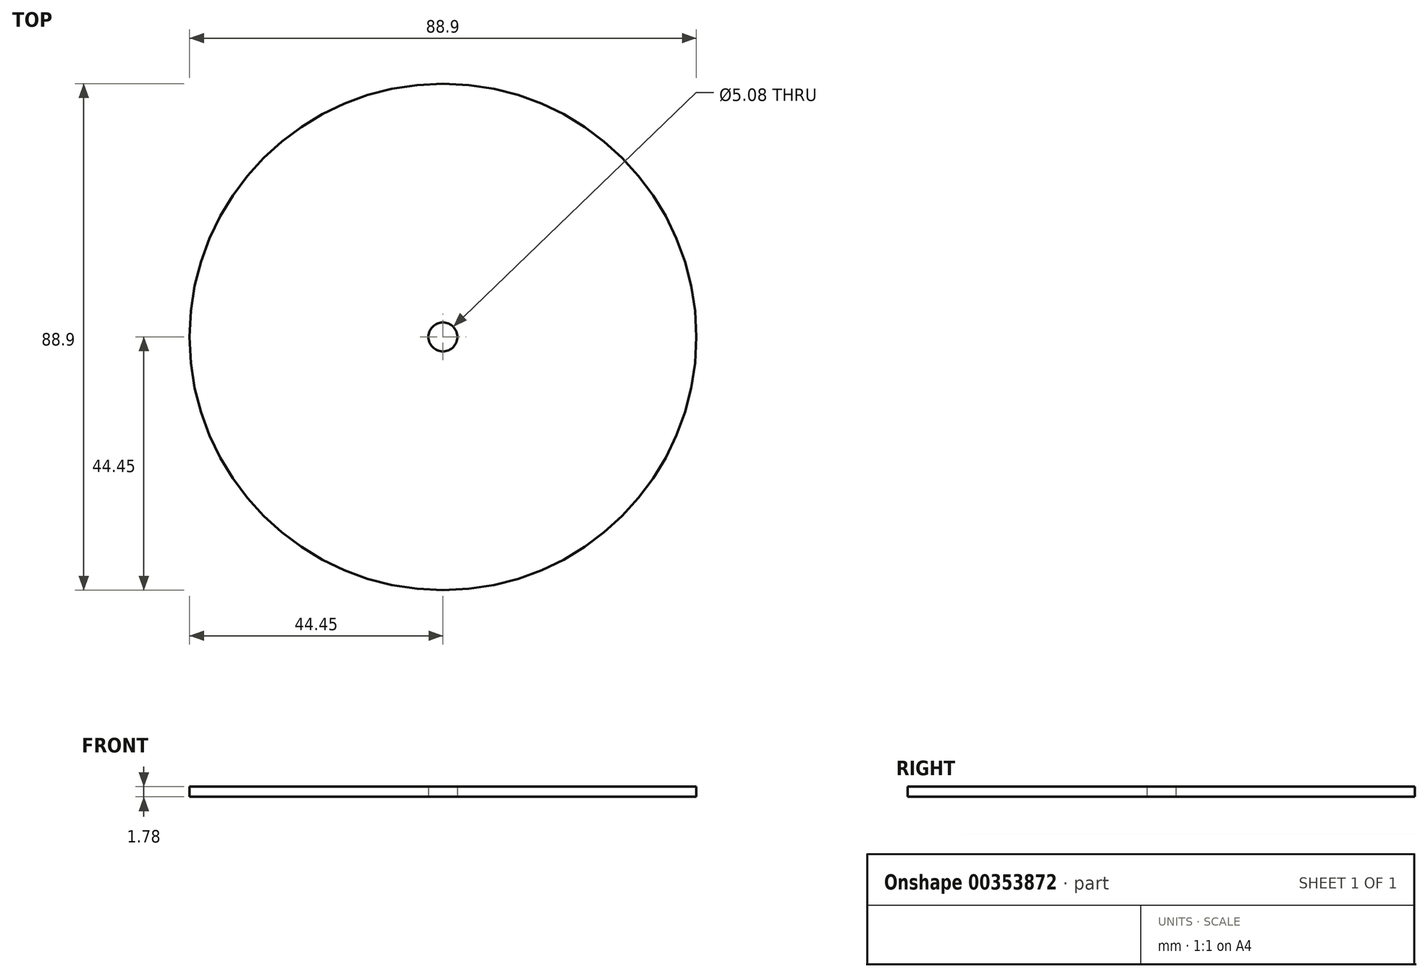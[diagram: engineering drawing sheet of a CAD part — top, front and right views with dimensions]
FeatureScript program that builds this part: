
annotation { "Feature Type Name" : "Feature", "Feature Type Description" : "" }
export const myFeature = defineFeature(function(context is Context, id is Id, definition is map)
    precondition{}
    {
        {
            var Q0;
            Q0=qCreatedBy(makeId("Top.planeOp"),FACE);
            var sketch = newSketch(context, id + "F0", { "sketchPlane" : qUnion([Q0])});
            skCircle(sketch, "E0", {"center": v(0, 0) * mm, "radius": 44.45 * mm});
            skCircle(sketch, "E1", {"center": v(0, 0) * mm, "radius": 2.54 * mm});
            skSolve(sketch);
        }
        {
            var Q0;
            Q0 = qSketchRegion(id + "F0", true);
            extrude(context, id + "F1", {"entities" : qUnion([Q0]), "depth" : 1.78 * mm});
        }
    });
